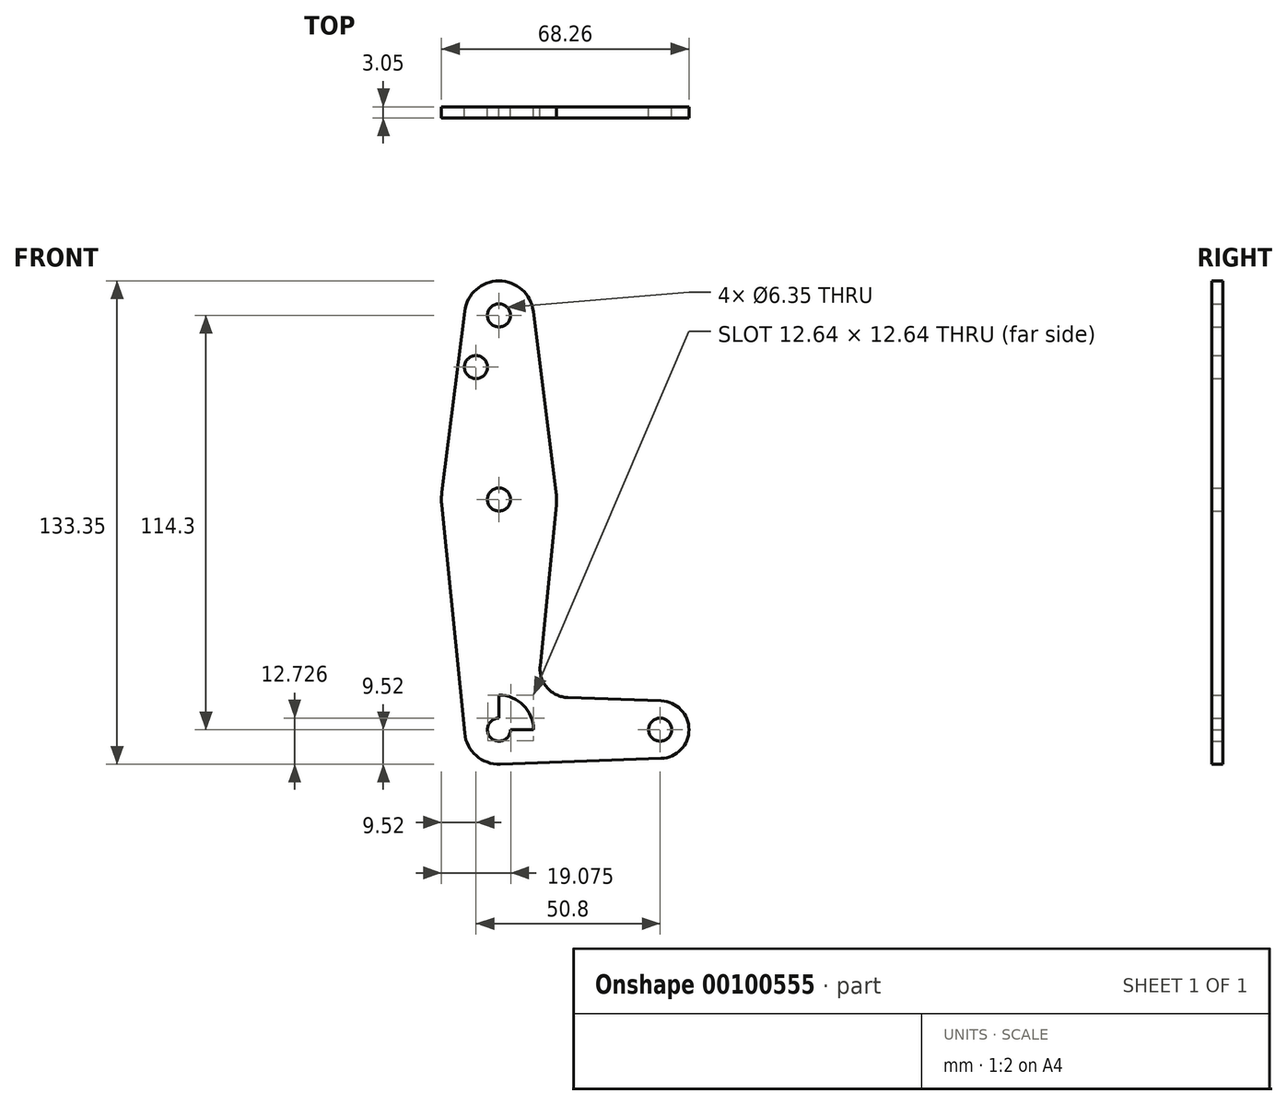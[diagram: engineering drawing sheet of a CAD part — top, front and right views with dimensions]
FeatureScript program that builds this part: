
annotation { "Feature Type Name" : "Feature", "Feature Type Description" : "" }
export const myFeature = defineFeature(function(context is Context, id is Id, definition is map)
    precondition{}
    {
        {
            var Q0;
            Q0=qCreatedBy(makeId("Front.planeOp"),FACE);
            var sketch = newSketch(context, id + "F0", { "sketchPlane" : qUnion([Q0])});
            skCircle(sketch, "E0", {"center": v(0, 114.3) * mm, "radius": 9.53 * mm});
            skCircle(sketch, "E1", {"center": v(0, 63.5) * mm, "radius": 15.88 * mm});
            skCircle(sketch, "E2", {"center": v(0, 0) * mm, "radius": 9.53 * mm});
            skLineSegment(sketch, "E3", {"start": v(0, 63.5) * mm, "end": v(0, 0) * mm});
            skLineSegment(sketch, "E4", {"start": v(0, 114.3) * mm, "end": v(0, 0) * mm});
            skLineSegment(sketch, "E5", {"start": v(0, 0) * mm, "end": v(44.45, 0) * mm});
            skLineSegment(sketch, "E6", {"start": v(9.45, 115.5) * mm, "end": v(15.75, 65.48) * mm});
            skLineSegment(sketch, "E7", {"start": v(-9.45, 115.5) * mm, "end": v(-15.75, 65.48) * mm});
            skLineSegment(sketch, "E8", {"start": v(15.8, 61.91) * mm, "end": v(11.34, 17.6) * mm});
            skCircle(sketch, "E9", {"center": v(44.45, 0) * mm, "radius": 7.94 * mm});
            skLineSegment(sketch, "E10", {"start": v(18.97, 8.85) * mm, "end": v(44.73, 7.93) * mm});
            skLineSegment(sketch, "E11", {"start": v(-15.8, 61.91) * mm, "end": v(-9.48, -0.95) * mm});
            skLineSegment(sketch, "E12", {"start": v(0.34, -9.52) * mm, "end": v(44.73, -7.93) * mm});
            skCircle(sketch, "E13", {"center": v(0, 114.3) * mm, "radius": 3.18 * mm});
            skCircle(sketch, "E14", {"center": v(0, 63.5) * mm, "radius": 3.18 * mm});
            skCircle(sketch, "E15", {"center": v(0, 0) * mm, "radius": 3.18 * mm});
            skCircle(sketch, "E16", {"center": v(44.45, 0) * mm, "radius": 3.18 * mm});
            skCircle(sketch, "E17", {"center": v(-6.35, 100.03) * mm, "radius": 3.18 * mm});
            skArc(sketch, "E18.filletArc", {"start": v(11.34, 17.6) * mm, "mid": v(13.26, 11.57) * mm, "end": v(18.97, 8.85) * mm});
            skSolve(sketch);
        }
        {
            var Q0;
            Q0=makeQuery(id+"F0.imprint","IMPRINT",FACE,{"disambiguationData":[TD([[makeQuery(id+"F0.imprint","IMPRINT",EDGE,{"derivedFrom":sQuery(id+"F0.wireOp",EDGE,"E13")}),-1.0]])]});
            var Q1;
            {var subQ0=sQuery(id+"F0.wireOp",EDGE,"E11");Q1=makeQuery(id+"F0.imprint","IMPRINT",FACE,{"disambiguationData":[TD([[makeQuery(id+"F0.imprint","IMPRINT",EDGE,{"derivedFrom":subQ0}),1.0]])]});}
            var Q2;
            {var subQ0=sQuery(id+"F0.wireOp",EDGE,"E12");Q2=makeQuery(id+"F0.imprint","IMPRINT",FACE,{"disambiguationData":[TD([[makeQuery(id+"F0.imprint","IMPRINT",EDGE,{"derivedFrom":subQ0}),1.0]])]});}
            var Q3;
            Q3=makeQuery(id+"F0.imprint","IMPRINT",FACE,{"disambiguationData":[TD([[makeQuery(id+"F0.imprint","IMPRINT",EDGE,{"derivedFrom":sQuery(id+"F0.wireOp",EDGE,"E16")}),-1.0]])]});
            var Q4;
            {var subQ0=sQuery(id+"F0.wireOp",EDGE,"E7");Q4=makeQuery(id+"F0.imprint","IMPRINT",FACE,{"disambiguationData":[TD([[makeQuery(id+"F0.imprint","IMPRINT",EDGE,{"derivedFrom":subQ0}),1.0]])]});}
            var Q5;
            {var subQ1=sQuery(id+"F0.wireOp",EDGE,"E1");var subQ7=makeQuery(id+"F0.imprint","INTERSECT",VERTEX,{"derivedFrom":[subQ1,sQuery(id+"F0.wireOp",EDGE,"E6")]});Q5=makeQuery(id+"F0.imprint","IMPRINT",FACE,{"disambiguationData":[TD([[makeQuery(id+"F0.imprint","IMPRINT",EDGE,{"disambiguationData":[TD([[subQ7,-1.0]])],"derivedFrom":subQ1}),1.0]])]});}
            var Q6;
            {var subQ1=sQuery(id+"F0.wireOp",EDGE,"E1");var subQ8=makeQuery(id+"F0.imprint","INTERSECT",VERTEX,{"derivedFrom":[subQ1,sQuery(id+"F0.wireOp",EDGE,"E7")]});Q6=makeQuery(id+"F0.imprint","IMPRINT",FACE,{"disambiguationData":[TD([[makeQuery(id+"F0.imprint","IMPRINT",EDGE,{"disambiguationData":[TD([[subQ8,1.0]])],"derivedFrom":subQ1}),1.0]])]});}
            var Q7;
            {var subQ1=sQuery(id+"F0.wireOp",EDGE,"E2");var subQ8=makeQuery(id+"F0.imprint","INTERSECT",VERTEX,{"derivedFrom":[subQ1,sQuery(id+"F0.wireOp",EDGE,"E11")]});Q7=makeQuery(id+"F0.imprint","IMPRINT",FACE,{"disambiguationData":[TD([[makeQuery(id+"F0.imprint","IMPRINT",EDGE,{"disambiguationData":[TD([[subQ8,1.0]])],"derivedFrom":subQ1}),1.0]])]});}
            var Q8;
            {var subQ9=sQuery(id+"F0.wireOp",EDGE,"E8");Q8=makeQuery(id+"F0.imprint","IMPRINT",FACE,{"disambiguationData":[TD([[makeQuery(id+"F0.imprint","IMPRINT",EDGE,{"derivedFrom":subQ9}),-1.0]])]});}
            var Q9;
            {var subQ0=sQuery(id+"F0.wireOp",EDGE,"E4");var subQ1=sQuery(id+"F0.wireOp",EDGE,"E2");var subQ2=makeQuery(id+"F0.imprint","INTERSECT",VERTEX,{"derivedFrom":[subQ1,subQ0]});Q9=makeQuery(id+"F0.imprint","IMPRINT",FACE,{"disambiguationData":[TD([[makeQuery(id+"F0.imprint","IMPRINT",EDGE,{"disambiguationData":[TD([[subQ2,1.0]])],"derivedFrom":subQ1}),1.0]])]});}
            var Q10;
            {var subQ0=sQuery(id+"F0.wireOp",EDGE,"E6");Q10=makeQuery(id+"F0.imprint","IMPRINT",FACE,{"disambiguationData":[TD([[makeQuery(id+"F0.imprint","IMPRINT",EDGE,{"derivedFrom":subQ0}),-1.0]])]});}
            extrude(context, id + "F1", {"entities" : qUnion([Q0, Q1, Q2, Q3, Q4, Q5, Q6, Q7, Q8, Q9, Q10]), "depth" : 3.05 * mm});
        }
    });
